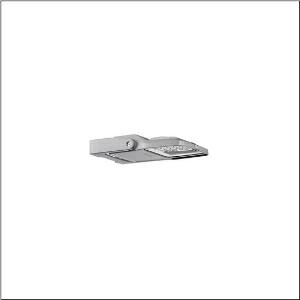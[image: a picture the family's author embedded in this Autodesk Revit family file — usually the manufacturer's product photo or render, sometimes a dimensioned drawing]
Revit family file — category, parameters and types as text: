
# Revit family: floodlight_fl_21_iq_micro___pl52_5xa7761a4d2a_29c7
name_source: partatom
category: Lighting Fixtures
units: mm (PartAtom-declared; Revit-internal decimal feet)

## family parameters
Cut with Voids When Loaded = No
Host = Face
Light Source = No
Part Type = Normal
Room Calculation Point = No
Round Connector Dimension = Use Diameter
Shared = No

## types (1)
- --- (1 x LED, 3010 lm, 23.1 W, 4000K)
    Apparent Load = 23 VA
    CIE Flux Codes = 26 60 98 100 100
    Color Rendering = 70
    Color Temperature = 4000K
    Default Elevation = 1800 mm
    Description = Floodlight FL 21 iQ micro, floodlight, primary light control with lens, of PMMA, primary optical cover: protective disc, of toughened safety glass, transparent, light distribution: PL52, light emission: direct distribution, installation type: surface-mounted, LED, High Power LED, rated luminous flux: 3.010lm, luminous efficacy: 130lm/W, light colour: 740, colour temperature: 4000K, control: optimised constant luminous flux control (CLO 2.0), Desk-Remote (wireless, voltage-free reading and setting of iQ features in the workshop via application-optimized NFC function/RFID function), Light-Fading, Smart-Wire, Night-Set, Lumen-Switch, Temp-Guard, Auto-Match, with terminal, 6-pole, mains connection: 220..240V, AC, 50/60Hz, start of lifetime: 23W, end of service life: 24W, reduction: 11W, luminaire housing, of diecast aluminium, powder-coated, Siteco® metallic grey (DB 702S), corrosivity category C5 mid according to DIN EN ISO 12944, sealing non-destructively replaceable, design bracket, of diecast aluminium, powder-coated, Siteco® metallic grey (DB 702S), protection rating (complete): IP66, insulation class (complete): insulation class II (safety insulation), certification: CE, ENEC, VDE, protection symbol: D, impact resistance: IK07, permissible operating ambient temperature: -40..+40°C, permissible operating ambient temperature for outdoor applications: -40..+50°C, standard: DIN EN 12944, LABS conformity tested according to VDMA 24364:2018-05, packaging unit: 1 piece

Light Distribution: PL52
    Height = 65 mm
    Lamp = 1 x LED
    Lamp Light Flux = 3010 lm
    Lamp Power = 23.1 W
    Lamp count = 1
    Length = 312 mm
    Luminous efficacy = 130 lm/W
    Manufacturer = Siteco
    ModVariant = No
    Model = 5XA7761A4D2A
    Mounting Place = Wall
    Mounting Type = Surface mounted
    Number of Poles = 1
    OnlyDefault = Yes
    Power Factor = 1
    Product Name = Floodlight FL 21 iQ micro | PL52
    Product group = floodlight | wall mounted
    ProductGroupID = 2001
    Protection Class = Protection class II
    Protection Degree = IP 66
    RLX_Detail_Level = 1
    RLX_Emergency_Light_Flux = 0 lm
    RLX_Emergency_Type = 0
    RLX_Emergency_Type_DB = No
    RlxData = <blob elided: 97433 chars, md5=2a4bd0f7>
    Socket = socket
    Standby Power = 0 W
    System Light Flux = 3010 lm
    System Power = 23 W
    Type Comments = factory setting: luminous flux: 100 % | dim-lin: 254 | 455 mA
    Type Image = l_1006878.jpg
    URL = http://relux.com
    VarID = @adj_110813
    Voltage = 0 V
    Weight = 0.00 kg
    Width = 230 mm

## geometry (parser evidence)
native form markers: Blend x4, Sweep x12
no freeform markers — native parametric forms only
